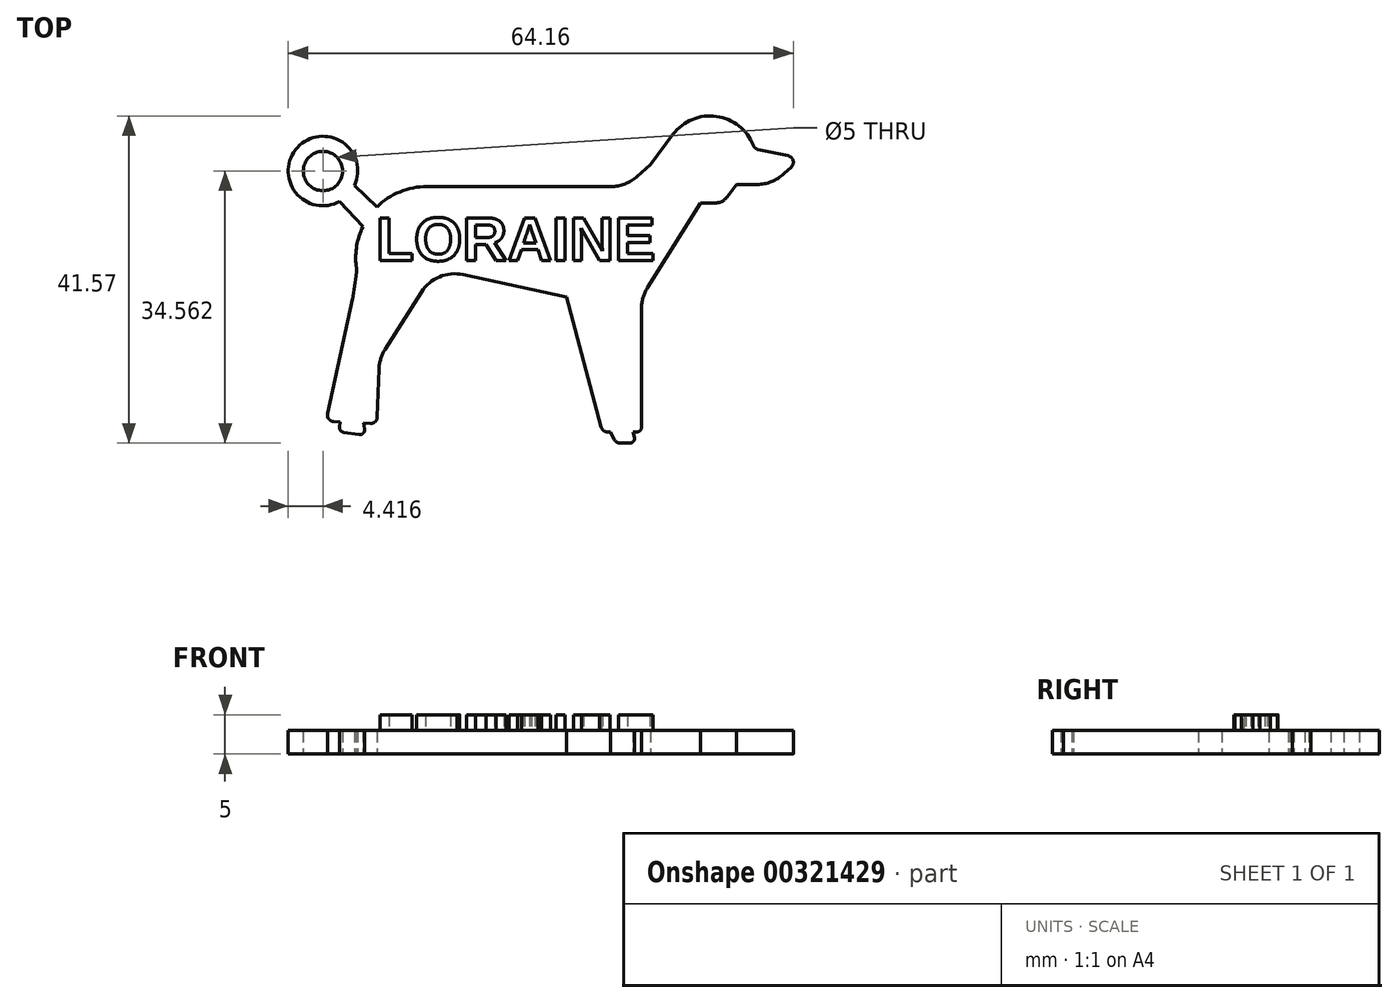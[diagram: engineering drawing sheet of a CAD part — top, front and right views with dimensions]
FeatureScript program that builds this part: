
annotation { "Feature Type Name" : "Feature", "Feature Type Description" : "" }
export const myFeature = defineFeature(function(context is Context, id is Id, definition is map)
    precondition{}
    {
        {
            var Q0;
            Q0=qCreatedBy(makeId("Top.planeOp"),FACE);
            var sketch = newSketch(context, id + "F0", { "sketchPlane" : qUnion([Q0])});
            skLineSegment(sketch, "E0.bottom", {"start": v(35, 25) * mm, "end": v(-35, 25) * mm});
            skLineSegment(sketch, "E0.top", {"start": v(35, -25) * mm, "end": v(-35, -25) * mm});
            skLineSegment(sketch, "E0.left", {"start": v(35, 25) * mm, "end": v(35, -25) * mm});
            skLineSegment(sketch, "E0.right", {"start": v(-35, 25) * mm, "end": v(-35, -25) * mm});
            skPoint(sketch, "E0.middle", {"position": v(0, 0) * mm});
            skLineSegment(sketch, "E1", {"start": v(31.2, 14.36) * mm, "end": v(27.37, 15.17) * mm});
            skLineSegment(sketch, "E2", {"start": v(16.58, 17.1) * mm, "end": v(13.7, 13.27) * mm});
            skLineSegment(sketch, "E3", {"start": v(13.7, 13.27) * mm, "end": v(12.01, 11.75) * mm});
            skLineSegment(sketch, "E4", {"start": v(8.66, 10.46) * mm, "end": v(-14.7, 10.46) * mm});
            skArc(sketch, "E5", {"start": v(-14.7, 10.46) * mm, "mid": v(-18.12, 9.78) * mm, "end": v(-21.03, 7.86) * mm});
            skLineSegment(sketch, "E6", {"start": v(-23.7, -0.93) * mm, "end": v(-24.06, -3.44) * mm});
            skLineSegment(sketch, "E7", {"start": v(-24.12, -3.78) * mm, "end": v(-27.32, -18.4) * mm});
            skLineSegment(sketch, "E8", {"start": v(31.59, 12.94) * mm, "end": v(30.66, 12.07) * mm});
            skLineSegment(sketch, "E9", {"start": v(27.24, 10.72) * mm, "end": v(24.61, 10.72) * mm});
            skLineSegment(sketch, "E10", {"start": v(24.61, 10.72) * mm, "end": v(23.5, 9.18) * mm});
            skLineSegment(sketch, "E11", {"start": v(21.88, 8.35) * mm, "end": v(20.08, 8.35) * mm});
            skLineSegment(sketch, "E12", {"start": v(20.08, 8.35) * mm, "end": v(13.34, -2.4) * mm});
            skLineSegment(sketch, "E13", {"start": v(12.57, -5.05) * mm, "end": v(12.57, -20.14) * mm});
            skLineSegment(sketch, "E14", {"start": v(11.97, -20.74) * mm, "end": v(11.5, -20.74) * mm});
            skLineSegment(sketch, "E15", {"start": v(7.45, -20.12) * mm, "end": v(3.03, -3.61) * mm});
            skLineSegment(sketch, "E16", {"start": v(3.03, -3.61) * mm, "end": v(-10.1, -0.75) * mm});
            skLineSegment(sketch, "E17", {"start": v(-26.55, -19.4) * mm, "end": v(-25.7, -19.45) * mm});
            skLineSegment(sketch, "E18", {"start": v(-25.7, -19.45) * mm, "end": v(-25.8, -20.08) * mm});
            skLineSegment(sketch, "E19", {"start": v(-21.03, 7.86) * mm, "end": v(-23.9, 10.57) * mm});
            skLineSegment(sketch, "E20", {"start": v(-22.83, 5.36) * mm, "end": v(-25.75, 8.56) * mm});
            skArc(sketch, "E21", {"start": v(-23.9, 10.57) * mm, "mid": v(-31.13, 15.43) * mm, "end": v(-25.75, 8.56) * mm});
            skLineSegment(sketch, "E22", {"start": v(-15.39, -2.95) * mm, "end": v(-20, -10.23) * mm});
            skLineSegment(sketch, "E23", {"start": v(-20.78, -12.73) * mm, "end": v(-21, -18.85) * mm});
            skLineSegment(sketch, "E24", {"start": v(8.66, -20.74) * mm, "end": v(9.1, -21.66) * mm});
            skLineSegment(sketch, "E25", {"start": v(11.5, -20.74) * mm, "end": v(11.67, -21.4) * mm});
            skLineSegment(sketch, "E26", {"start": v(11.08, -22.14) * mm, "end": v(9.85, -22.14) * mm});
            skLineSegment(sketch, "E27", {"start": v(-25.29, -20.76) * mm, "end": v(-23.3, -21.06) * mm});
            skLineSegment(sketch, "E28", {"start": v(-22.62, -20.37) * mm, "end": v(-22.74, -19.6) * mm});
            skPoint(sketch, "E29.orphan", {"position": v(-25.88, 8.7) * mm});
            skPoint(sketch, "E30.orphan", {"position": v(-25.88, 12.46) * mm});
            skArc(sketch, "E31.trimOffspring", {"start": v(-22.83, 5.36) * mm, "mid": v(-23.6, 2.93) * mm, "end": v(-23.67, 0.38) * mm});
            skCircle(sketch, "E32", {"center": v(-27.9, 12.42) * mm, "radius": 2.5 * mm});
            skPoint(sketch, "E33.visualSharp", {"position": v(-13.52, 0) * mm});
            skArc(sketch, "E33.filletArc", {"start": v(-10.1, -0.75) * mm, "mid": v(-13.1, -1.02) * mm, "end": v(-15.39, -2.95) * mm});
            skPoint(sketch, "E34.visualSharp", {"position": v(-20.74, -11.38) * mm});
            skArc(sketch, "E34.filletArc", {"start": v(-20, -10.23) * mm, "mid": v(-20.56, -11.43) * mm, "end": v(-20.78, -12.73) * mm});
            skPoint(sketch, "E35.visualSharp", {"position": v(-23.59, -0.2) * mm});
            skArc(sketch, "E35.filletArc", {"start": v(-23.7, -0.93) * mm, "mid": v(-23.64, -0.28) * mm, "end": v(-23.67, 0.38) * mm});
            skPoint(sketch, "E36.visualSharp", {"position": v(-24.09, -3.61) * mm});
            skArc(sketch, "E36.filletArc", {"start": v(-24.12, -3.78) * mm, "mid": v(-24.09, -3.61) * mm, "end": v(-24.06, -3.44) * mm});
            skPoint(sketch, "E37.visualSharp", {"position": v(12.57, -3.61) * mm});
            skArc(sketch, "E37.filletArc", {"start": v(13.34, -2.4) * mm, "mid": v(12.77, -3.67) * mm, "end": v(12.57, -5.05) * mm});
            skPoint(sketch, "E38.visualSharp", {"position": v(10.58, 10.46) * mm});
            skArc(sketch, "E38.filletArc", {"start": v(8.66, 10.46) * mm, "mid": v(10.46, 10.79) * mm, "end": v(12.01, 11.75) * mm});
            skPoint(sketch, "E39.visualSharp", {"position": v(32.75, 14.03) * mm});
            skArc(sketch, "E39.filletArc", {"start": v(31.59, 12.94) * mm, "mid": v(31.82, 13.77) * mm, "end": v(31.2, 14.36) * mm});
            skPoint(sketch, "E40.visualSharp", {"position": v(29.22, 10.72) * mm});
            skArc(sketch, "E40.filletArc", {"start": v(27.24, 10.72) * mm, "mid": v(29.08, 11.07) * mm, "end": v(30.66, 12.07) * mm});
            skPoint(sketch, "E41.visualSharp", {"position": v(26.18, 15.42) * mm});
            skArc(sketch, "E41.filletArc", {"start": v(26.77, 15.68) * mm, "mid": v(27, 15.35) * mm, "end": v(27.37, 15.17) * mm});
            skLineSegment(sketch, "E42.trimOffspring", {"start": v(-22.74, -19.6) * mm, "end": v(-21.88, -19.65) * mm});
            skPoint(sketch, "E43.visualSharp", {"position": v(-27.53, -19.35) * mm});
            skArc(sketch, "E43.filletArc", {"start": v(-27.32, -18.4) * mm, "mid": v(-27.17, -19.07) * mm, "end": v(-26.55, -19.4) * mm});
            skPoint(sketch, "E44.visualSharp", {"position": v(-21.03, -19.7) * mm});
            skArc(sketch, "E44.filletArc", {"start": v(-21.88, -19.65) * mm, "mid": v(-21.27, -19.43) * mm, "end": v(-21, -18.85) * mm});
            skPoint(sketch, "E45.visualSharp", {"position": v(-22.48, -21.18) * mm});
            skArc(sketch, "E45.filletArc", {"start": v(-23.3, -21.06) * mm, "mid": v(-22.78, -20.88) * mm, "end": v(-22.62, -20.37) * mm});
            skPoint(sketch, "E46.visualSharp", {"position": v(-25.88, -20.68) * mm});
            skArc(sketch, "E46.filletArc", {"start": v(-25.8, -20.08) * mm, "mid": v(-25.68, -20.53) * mm, "end": v(-25.29, -20.76) * mm});
            skLineSegment(sketch, "E47.trimOffspring", {"start": v(8.66, -20.74) * mm, "end": v(8.25, -20.74) * mm});
            skPoint(sketch, "E48.visualSharp", {"position": v(7.62, -20.74) * mm});
            skArc(sketch, "E48.filletArc", {"start": v(7.45, -20.12) * mm, "mid": v(7.75, -20.57) * mm, "end": v(8.25, -20.74) * mm});
            skPoint(sketch, "E49.visualSharp", {"position": v(12.57, -20.74) * mm});
            skArc(sketch, "E49.filletArc", {"start": v(11.97, -20.74) * mm, "mid": v(12.4, -20.56) * mm, "end": v(12.57, -20.14) * mm});
            skPoint(sketch, "E50.visualSharp", {"position": v(11.84, -22.14) * mm});
            skArc(sketch, "E50.filletArc", {"start": v(11.08, -22.14) * mm, "mid": v(11.55, -21.9) * mm, "end": v(11.67, -21.4) * mm});
            skPoint(sketch, "E51.visualSharp", {"position": v(9.32, -22.14) * mm});
            skArc(sketch, "E51.filletArc", {"start": v(9.1, -21.66) * mm, "mid": v(9.4, -22) * mm, "end": v(9.85, -22.14) * mm});
            skArc(sketch, "E52", {"start": v(26.77, 15.68) * mm, "mid": v(22.1, 19.37) * mm, "end": v(16.58, 17.1) * mm});
            skPoint(sketch, "E53.visualSharp", {"position": v(22.9, 8.35) * mm});
            skArc(sketch, "E53.filletArc", {"start": v(21.88, 8.35) * mm, "mid": v(22.8, 8.57) * mm, "end": v(23.5, 9.18) * mm});
            skSolve(sketch);
        }
        {
            var Q0;
            Q0=makeQuery(id+"F0.imprint","IMPRINT",FACE,{"disambiguationData":[TD([[makeQuery(id+"F0.imprint","IMPRINT",EDGE,{"derivedFrom":sQuery(id+"F0.wireOp",EDGE,"E1")}),1.0]])]});
            extrude(context, id + "F1", {"entities" : qUnion([Q0]), "depth" : 3 * mm});
        }
        {
            var Q0;
            Q0=makeQuery(id+"F1.opExtrude","CAP_FACE",FACE,{"disambiguationData":[OSD([sQuery(id+"F0.wireOp",EDGE,"E1"),sQuery(id+"F0.wireOp",EDGE,"E2"),sQuery(id+"F0.wireOp",EDGE,"E3"),sQuery(id+"F0.wireOp",EDGE,"E4"),sQuery(id+"F0.wireOp",EDGE,"E5"),sQuery(id+"F0.wireOp",EDGE,"E6"),sQuery(id+"F0.wireOp",EDGE,"E7"),sQuery(id+"F0.wireOp",EDGE,"E8"),sQuery(id+"F0.wireOp",EDGE,"E9"),sQuery(id+"F0.wireOp",EDGE,"E10"),sQuery(id+"F0.wireOp",EDGE,"E11"),sQuery(id+"F0.wireOp",EDGE,"E12"),sQuery(id+"F0.wireOp",EDGE,"E13"),sQuery(id+"F0.wireOp",EDGE,"E14"),sQuery(id+"F0.wireOp",EDGE,"E15"),sQuery(id+"F0.wireOp",EDGE,"E16"),sQuery(id+"F0.wireOp",EDGE,"E17"),sQuery(id+"F0.wireOp",EDGE,"E18"),sQuery(id+"F0.wireOp",EDGE,"E19"),sQuery(id+"F0.wireOp",EDGE,"E20"),sQuery(id+"F0.wireOp",EDGE,"E21"),sQuery(id+"F0.wireOp",EDGE,"E22"),sQuery(id+"F0.wireOp",EDGE,"E23"),sQuery(id+"F0.wireOp",EDGE,"E24"),sQuery(id+"F0.wireOp",EDGE,"E25"),sQuery(id+"F0.wireOp",EDGE,"E26"),sQuery(id+"F0.wireOp",EDGE,"E27"),sQuery(id+"F0.wireOp",EDGE,"E28"),sQuery(id+"F0.wireOp",EDGE,"E31.trimOffspring"),sQuery(id+"F0.wireOp",EDGE,"E32"),sQuery(id+"F0.wireOp",EDGE,"E33.filletArc"),sQuery(id+"F0.wireOp",EDGE,"E34.filletArc"),sQuery(id+"F0.wireOp",EDGE,"E35.filletArc"),sQuery(id+"F0.wireOp",EDGE,"E36.filletArc"),sQuery(id+"F0.wireOp",EDGE,"E37.filletArc"),sQuery(id+"F0.wireOp",EDGE,"E38.filletArc"),sQuery(id+"F0.wireOp",EDGE,"E39.filletArc"),sQuery(id+"F0.wireOp",EDGE,"E40.filletArc"),sQuery(id+"F0.wireOp",EDGE,"E41.filletArc"),sQuery(id+"F0.wireOp",EDGE,"E42.trimOffspring"),sQuery(id+"F0.wireOp",EDGE,"E43.filletArc"),sQuery(id+"F0.wireOp",EDGE,"E44.filletArc"),sQuery(id+"F0.wireOp",EDGE,"E45.filletArc"),sQuery(id+"F0.wireOp",EDGE,"E46.filletArc"),sQuery(id+"F0.wireOp",EDGE,"E47.trimOffspring"),sQuery(id+"F0.wireOp",EDGE,"E48.filletArc"),sQuery(id+"F0.wireOp",EDGE,"E49.filletArc"),sQuery(id+"F0.wireOp",EDGE,"E50.filletArc"),sQuery(id+"F0.wireOp",EDGE,"E51.filletArc"),sQuery(id+"F0.wireOp",EDGE,"E52"),sQuery(id+"F0.wireOp",EDGE,"E53.filletArc")])],"isStart":false});
            var sketch = newSketch(context, id + "F2", { "sketchPlane" : qUnion([Q0])});
            skText(sketch, "E54", { "text": "LORAINE", "fontName": "Arimo-Bold.ttf"});
            const initialGuessF2  = {"E54": [-0.02114, 0.00103, 1, 0, 0.00568]};
            skSetInitialGuess(sketch, initialGuessF2);
            skSolve(sketch);
        }
        {
            var Q0;
            Q0 = qSketchRegion(id + "F2", true);
            extrude(context, id + "F3", {"entities" : qUnion([Q0]), "operationType" : NewBodyOperationType.ADD, "depth" : 2 * mm});
        }
    });
